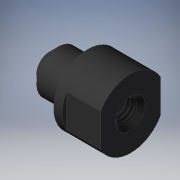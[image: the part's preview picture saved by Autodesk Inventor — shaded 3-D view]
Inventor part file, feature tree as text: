
AUTODESK INVENTOR PART (.ipt)
format: ipt  version: 2019 (Build 230136000, 136)  size: 144,384 bytes
history: native  units: mm
features: other x7, sketch x3, revolve x1, hole x1, extrude x1
ambient origin geometry x8: Origin, YZ Plane, XZ Plane, XY Plane, X Axis, Y Axis, Z Axis, Center Point
bodies: Solid1 (feature_tree)
feature tree (13):
  revolve  "Revolution1"  [1 undecoded]
  hole  "Hole1"  [1 undecoded]
  extrude  "Extrusion1"  [1 undecoded]
  other  "core_rod_XY"
  other  "core_rod_YZ"
  other  "core_rod_ZX"
  other  "core_rod_X"
  other  "core_rod_Y"
  other  "core_rod_Z"
  other  "core_rod_Center"
  sketch  "Sketch_1"  dims[d0=360.0deg]
  sketch  "Sketch2"  dims[d1=2.459mm d2=4.5mm d3=3.459mm d4=2.0mm d5=90.0deg d6=7.790148mm d7=120.0deg d8=4.0mm d9=0.0mm]
  sketch  "Sketch_2"  dims[d10=0.0mm]
note: 3 required parameter values undecoded (feature->parameter linkage not recoverable at this tier; creation-order binding heuristic only, values carry confidence <= 0.55)